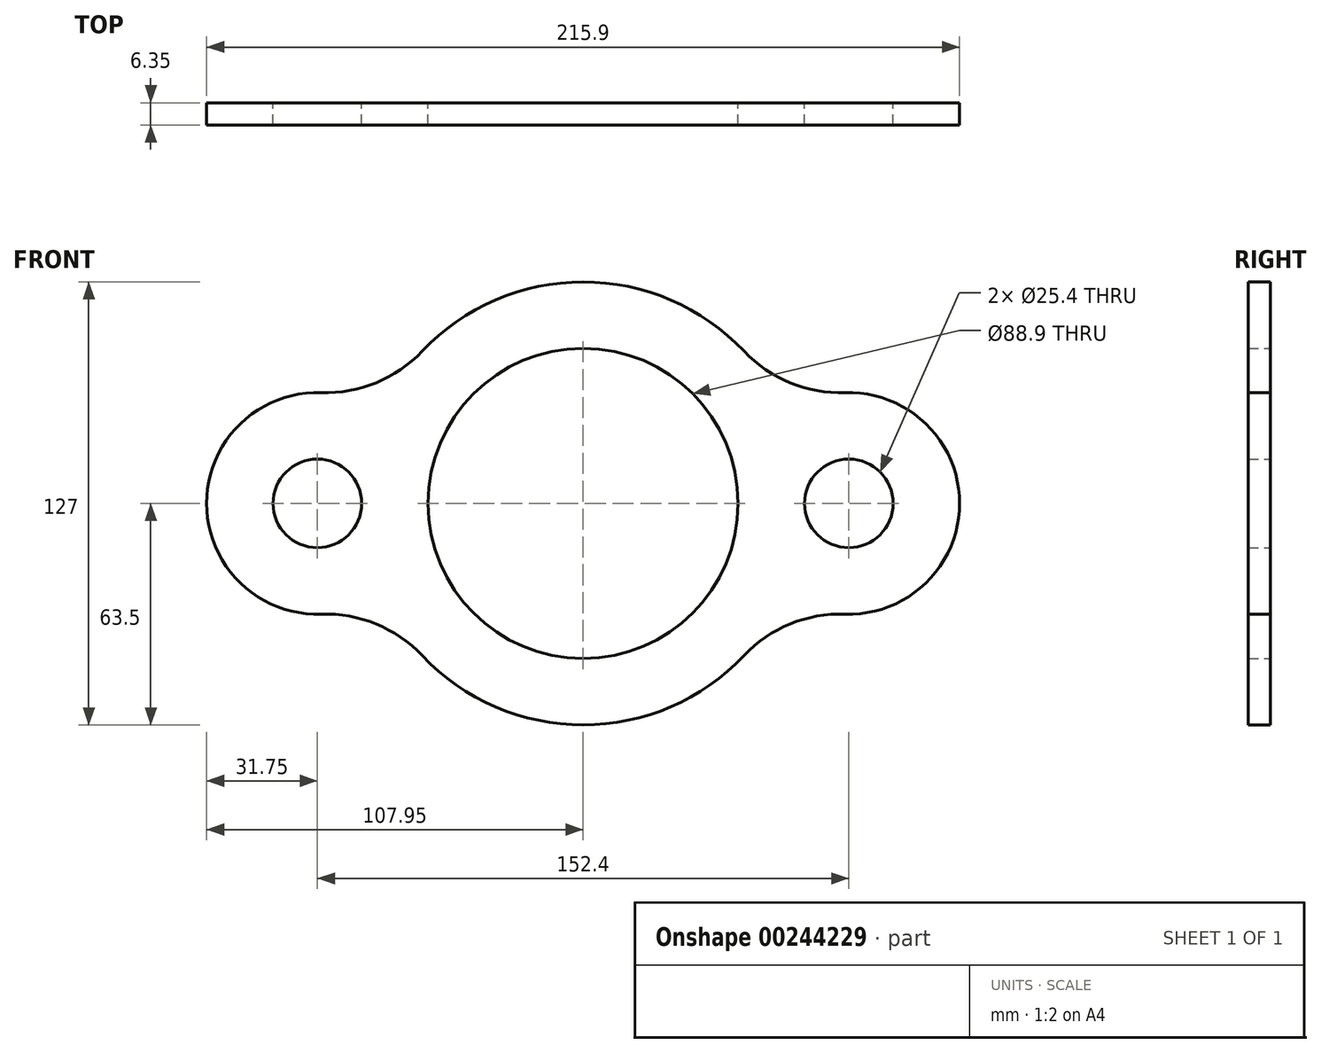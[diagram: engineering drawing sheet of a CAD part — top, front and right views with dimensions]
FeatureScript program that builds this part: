
annotation { "Feature Type Name" : "Feature", "Feature Type Description" : "" }
export const myFeature = defineFeature(function(context is Context, id is Id, definition is map)
    precondition{}
    {
        {
            var Q0;
            Q0=qCreatedBy(makeId("Front.planeOp"),FACE);
            var sketch = newSketch(context, id + "F0", { "sketchPlane" : qUnion([Q0])});
            skCircle(sketch, "E0", {"center": v(0, 0) * mm, "radius": 44.45 * mm});
            skArc(sketch, "E1", {"start": v(46.14, 43.63) * mm, "mid": v(0, 63.5) * mm, "end": v(-46.14, 43.63) * mm});
            skArc(sketch, "E2", {"start": v(-75.12, 31.73) * mm, "mid": v(-107.95, 0) * mm, "end": v(-75.12, -31.73) * mm});
            skCircle(sketch, "E3", {"center": v(-76.2, 0) * mm, "radius": 12.7 * mm});
            skArc(sketch, "E4", {"start": v(75.12, -31.73) * mm, "mid": v(107.95, 0) * mm, "end": v(75.12, 31.73) * mm});
            skCircle(sketch, "E5", {"center": v(76.2, 0) * mm, "radius": 12.7 * mm});
            skArc(sketch, "E6.trimOffspring", {"start": v(-46.14, -43.63) * mm, "mid": v(0, -63.5) * mm, "end": v(46.14, -43.63) * mm});
            skPoint(sketch, "E7.visualSharp", {"position": v(-57.94, 25.98) * mm});
            skArc(sketch, "E7.filletArc", {"start": v(-75.12, 31.73) * mm, "mid": v(-59.35, 34.56) * mm, "end": v(-46.14, 43.63) * mm});
            skPoint(sketch, "E8.visualSharp", {"position": v(-57.94, -25.98) * mm});
            skArc(sketch, "E8.filletArc", {"start": v(-46.14, -43.63) * mm, "mid": v(-59.35, -34.56) * mm, "end": v(-75.12, -31.73) * mm});
            skPoint(sketch, "E9.visualSharp", {"position": v(57.94, -25.98) * mm});
            skArc(sketch, "E9.filletArc", {"start": v(75.12, -31.73) * mm, "mid": v(59.35, -34.56) * mm, "end": v(46.14, -43.63) * mm});
            skPoint(sketch, "E10.visualSharp", {"position": v(57.94, 25.98) * mm});
            skArc(sketch, "E10.filletArc", {"start": v(46.14, 43.63) * mm, "mid": v(59.35, 34.56) * mm, "end": v(75.12, 31.73) * mm});
            skSolve(sketch);
        }
        {
            var Q0;
            Q0=makeQuery(id+"F0.imprint","IMPRINT",FACE,{"disambiguationData":[TD([[makeQuery(id+"F0.imprint","IMPRINT",EDGE,{"derivedFrom":sQuery(id+"F0.wireOp",EDGE,"E0")}),-1.0]])]});
            extrude(context, id + "F1", {"entities" : qUnion([Q0]), "depth" : 6.35 * mm});
        }
    });
